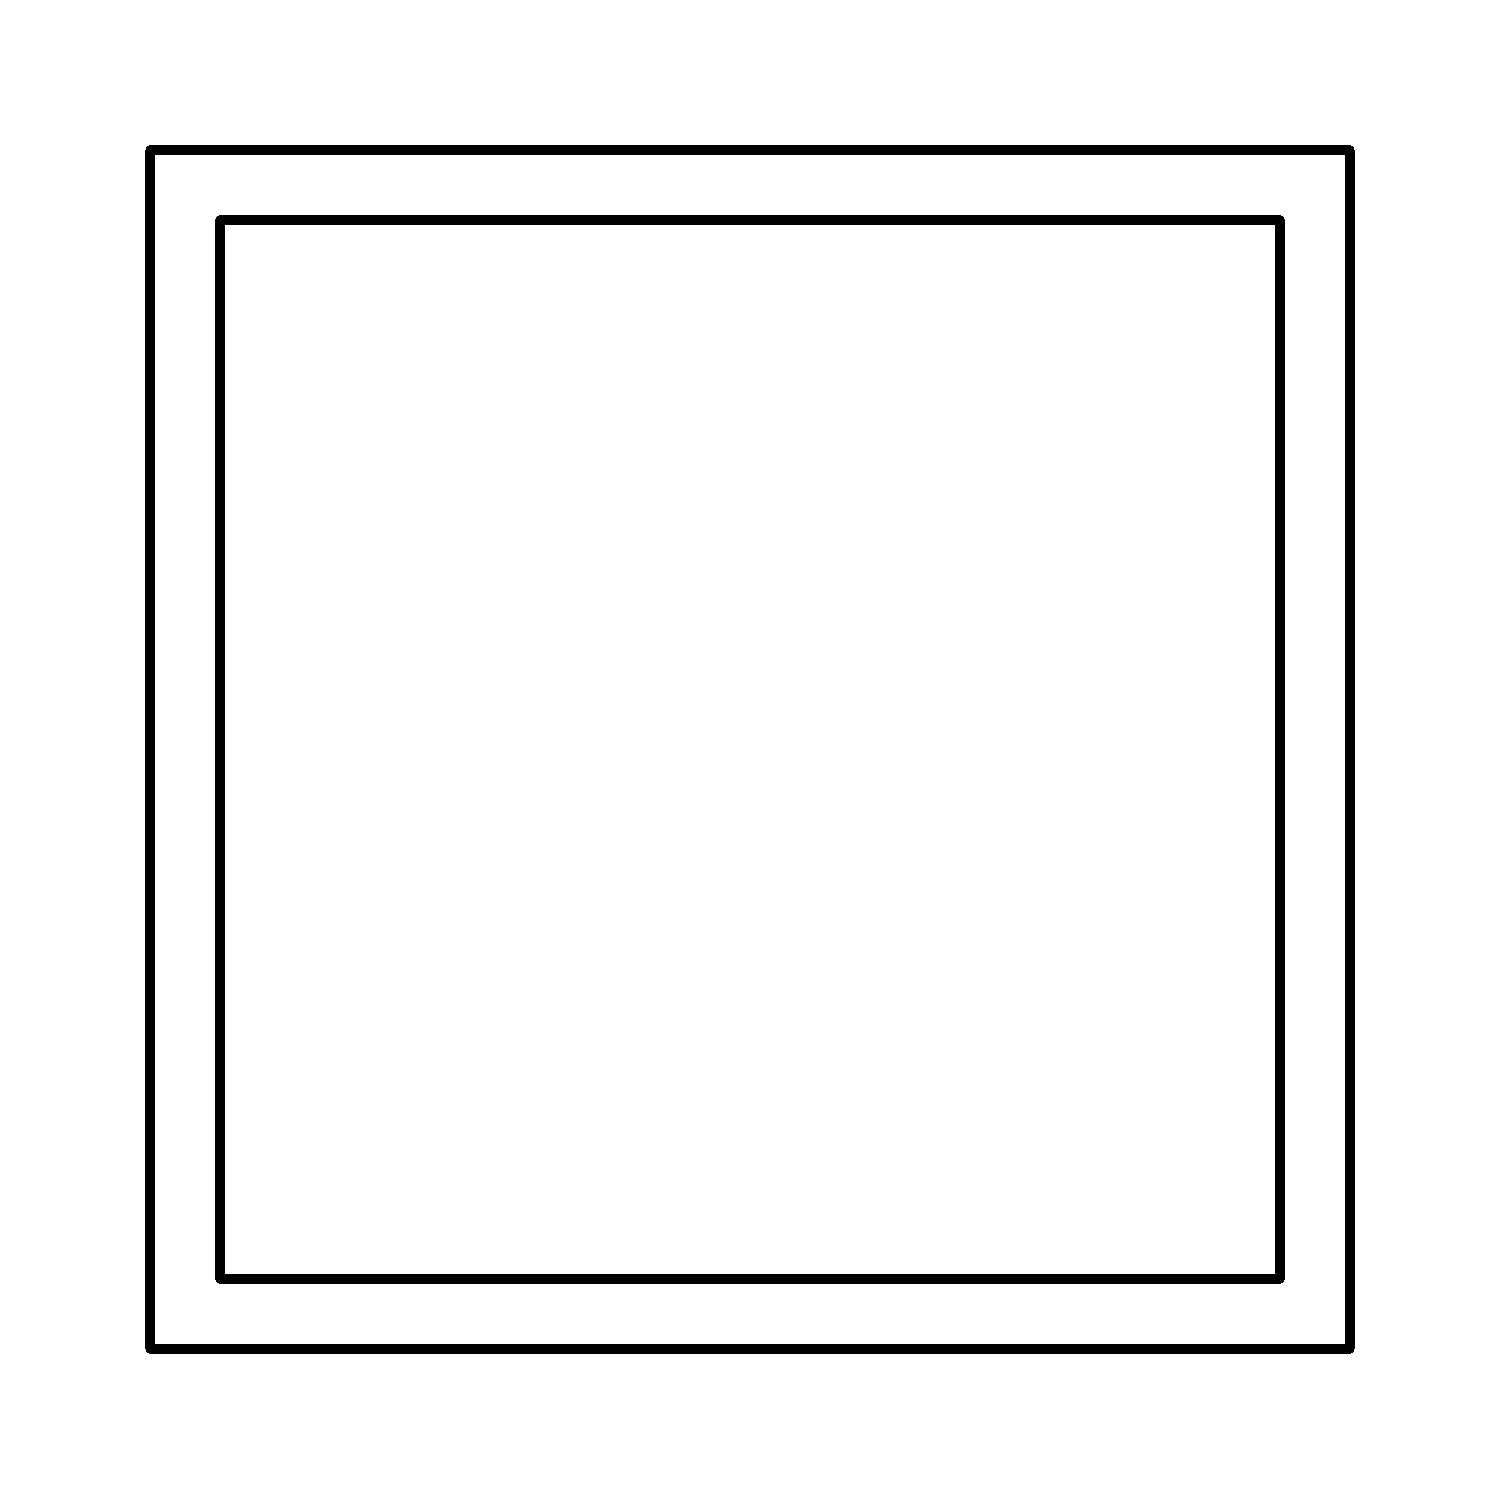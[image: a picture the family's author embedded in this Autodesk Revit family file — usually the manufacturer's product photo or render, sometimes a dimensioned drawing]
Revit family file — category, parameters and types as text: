
# Revit family: Окно.Alumark_одностворчатое_S44
name_source: partatom
category: Окна
revit_build: Autodesk Revit 2017 (Build: 20171027_0315(x64)
units: mm (PartAtom-declared; Revit-internal decimal feet)

## family parameters
Всегда вертикально = Да
Заголовок OmniClass = Windows
Номер OmniClass = 23.30.20.00
Общий = Нет
Основа = Стена
При загрузке вырезать с полостями = Нет
Точка расчета площади = Нет

## types (3) — shared parameters
#_рамы = 1000000
ADSK_Завод-изготовитель = ТБМ
ADSK_Обозначение = ГОСТ 21519-2003
URL = http://www.tbm.ru
sp_energy = Энергосберегающие стекла
sp_gaz = Заполненный газом
sp_standart = Обычный стеклопакет
Автоматический подбор рамы и створки = Да
Аналитическая конструкция = Окна с одинарным остеклением - для жилых зданий
Высота подоконника по умолчанию = 900 мм
Замыкание стены = По основе
Заполнение стеклопакета = Обычный стеклопакет
Изготовитель = ТБМ
Изображение типоразмера = схема_однопольное.png
Коэффициент теплопередачи (U) = 5.7361 Вт/(м²·K)
Коэффициент теплопритока от солнечного излучения = 0.86
Материал отлива = <По категории>
Материал подоконника = <По категории>
Материал рамы/створки = <По категории>
Материал стекла = <По категории>
Материал фурнитуры = <По категории>
Описание = Окно Проем ТБМ
Примерная высота = 960 мм
Примерная ширина = 660 мм
Пропускание видимого света = 0.9
Разработчик = ООО ПРОРУБИМ
Разработчик (телефон) = +7(495)649-85-43
ТБМ_Артикул_Клей = KMR0014
ТБМ_Артикул_Подкладка под СП = ALM740307
ТБМ_Артикул_Рама = ALM244101
ТБМ_Артикул_Распорный штифт = ALM885010
ТБМ_Артикул_Угловой соединитель рамы = ALM420011
ТБМ_Артикул_Уголок выравнивающий = ALM744014
ТБМ_Артикул_Уплотнитель внутренний = ALM770207
ТБМ_Артикул_Уплотнитель наружный = ALM770004
ТБМ_Артикул_Штапик = ALM244013
ТБМ_Длина_Рама = 3240 мм
ТБМ_Количество_Подкладка под СП = 6
ТБМ_Количество_Угловой соединитель рамы = 4
ТБМ_Соответствие рекомендациям = Размеры окна соответствует рекомендациям компании ТБМ
Термостойкость = 0.1743 (м²·K)/Вт
Тип рамы = Рама оконная : 44/26 мм (ALM244101)
Тип створки = Створка оконная : 32/43 мм (ALM244201)
Тип стеклопакета = 16мм 1-камерный
глухая_створка = Окна.Alumark_створка_однопольная (S44) : Глухая
обозначение_проема_высота = 160 мм
обозначение_проема_ширина = 110 мм
профиль створки_ширина = 43 мм
размер_X = 43 мм
размер_Y = 20 мм
размер_Z = 26 мм
рама_тип-1 = Рама оконная : 44/26 мм (ALM244101)
рама_тип-2 = Рама оконная : 60/42 мм (ALM244102)
рама_толщина = 44 мм
рама_ширина = 44 мм
сп_16_мм = 16мм 1-камерный
сп_24_мм = 24мм 1-камерный
створка_высота = 872 мм
створка_тип1 = Створка оконная : 32/43 мм (ALM244201)
створка_тип2 = Створка оконная : 48/59 мм (ALM244202)
створка_ширина = 572 мм
таблица выбора = Каталог_окна_S44
штапик_толщина = 28 мм
штапик_ширина = 18 мм

## per-type parameters (varying)
| type | #_створки | ADSK_Наименование | Створка | ТБМ_Артикул_Отлив | ТБМ_Артикул_Створка | ТБМ_Артикул_Угловой соединитель створки | ТБМ_Артикул_Уголок жесткости | ТБМ_Артикул_Уплотнитель притвора | ТБМ_Длина_Отлив | ТБМ_Длина_Створка | ТБМ_Длина_Уплотнитель внутренний | ТБМ_Длина_Уплотнитель наружный | ТБМ_Длина_Уплотнитель притвора | ТБМ_Длина_Штапик | ТБМ_Количество_Распорный штифт | ТБМ_Количество_Угловой соединитель створки | ТБМ_Количество_Уголок выравнивающий | ТБМ_Количество_Уголок жесткости | ТБМ_Площадь стеклопакета | ТБМ_Расход_Клей | ТБМ_Стеклопакет_Высота 1 | ТБМ_Стеклопакет_Ширина 1 | номер профиля |
| 660х960 (левое-откидное) | 10000 | ОАК (Профиль рамы 44/26 мм. Профиль створки 32/43 мм) СПО (Обычный стеклопакет 16 мм) | Окна.Alumark_створка_однопольная (S44) : Левая-откидная | ALM460035-1.07 | ALM244201 | ALM420011 | ALM744501 | ALM770001 | 560 мм | 3080 мм | 3080 мм | 3080 мм | 3080 мм | 2736 мм | 32 | 4 | 8 | 4 | 0.43 м² | 62 | 826 мм | 526 мм | 1010101 |
| 660х960 (глухое) | 0 | ОАК (Профиль рамы 44/26 мм) СПО (Обычный стеклопакет 16 мм) | Окна.Alumark_створка_однопольная (S44) : Глухая |  |  |  |  |  | 0 мм | 0 мм | 3240 мм | 3240 мм | 0 мм | 3032 мм | 16 | 0 | 4 | 0 | 0.53 м² | 28 | 894 мм | 594 мм | 1000101 |
| 960х960 (правое-откидное) | 10000 | ОАК (Профиль рамы 44/26 мм. Профиль створки 32/43 мм) СПО (Обычный стеклопакет 16 мм) | Окна.Alumark_створка_однопольная (S44) : Правая-откидная | ALM460035-1.07 | ALM244201 | ALM420011 | ALM744501 | ALM770001 | 560 мм | 3080 мм | 3080 мм | 3080 мм | 3080 мм | 2736 мм | 32 | 4 | 8 | 4 | 0.43 м² | 62 | 826 мм | 526 мм | 1010101 |
